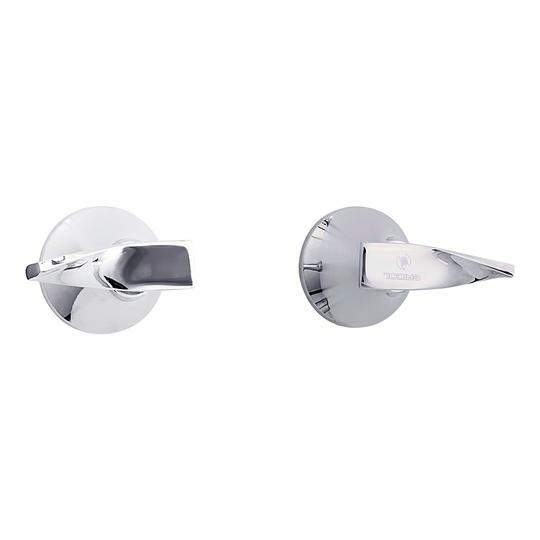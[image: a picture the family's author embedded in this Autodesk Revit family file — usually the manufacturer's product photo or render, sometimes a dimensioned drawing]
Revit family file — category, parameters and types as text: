
# Revit family: 01-2835-11SR-MEZCLADOR 8 SST PRISTINA
name_source: partatom
category: Aparatos sanitarios
revit_build: Autodesk Revit 2018 (Build: 20170223_1515(x64)
units: mm (PartAtom-declared; Revit-internal decimal feet)

## family parameters
Anfitrión = Cara
Compartido = No
Corte con vacíos al cargar = No
Cota de conector redondo = Diámetro de uso
Número OmniClass = 23.31.11.00
Punto de cálculo de habitación = No
Tipo de pieza = Normal

## types (1)
- 01-2835-11SR
    Alto = 60 mm  [stored 0.19685 ft]
    Ancho = 60 mm  [stored 0.19685 ft]
    Conexión AC = Sí
    Conexión AF = Sí
    Conexión de residuos = No
    Conexión de ventilación = No
    Descripción = Mezclador ducha
    Distancia entre griferias = 203 mm
    Elevación por defecto = 0 mm  [stored 0 ft]
    Fabricante = Gricol
    Imagen de tipo = <Ninguno>
    Link Ficha Tecnica = http://infotecnica.gricol.com
    Mezclador = Mezclador
    Modelo = 01-2835-11SR
    Plastico ABS Cromado = Plastico ABS Cromado
    Product Name = MEZCLADOR 8 SST PRISTINA
    Profundidad = 210 mm
    URL = https://www.gricol.com

note: [stored X ft] marks values corroborated as IEEE doubles in the binary element streams (Revit-internal decimal feet)

## geometry (parser evidence)
native form markers: Blend x2, Sweep x4
no freeform markers — native parametric forms only
